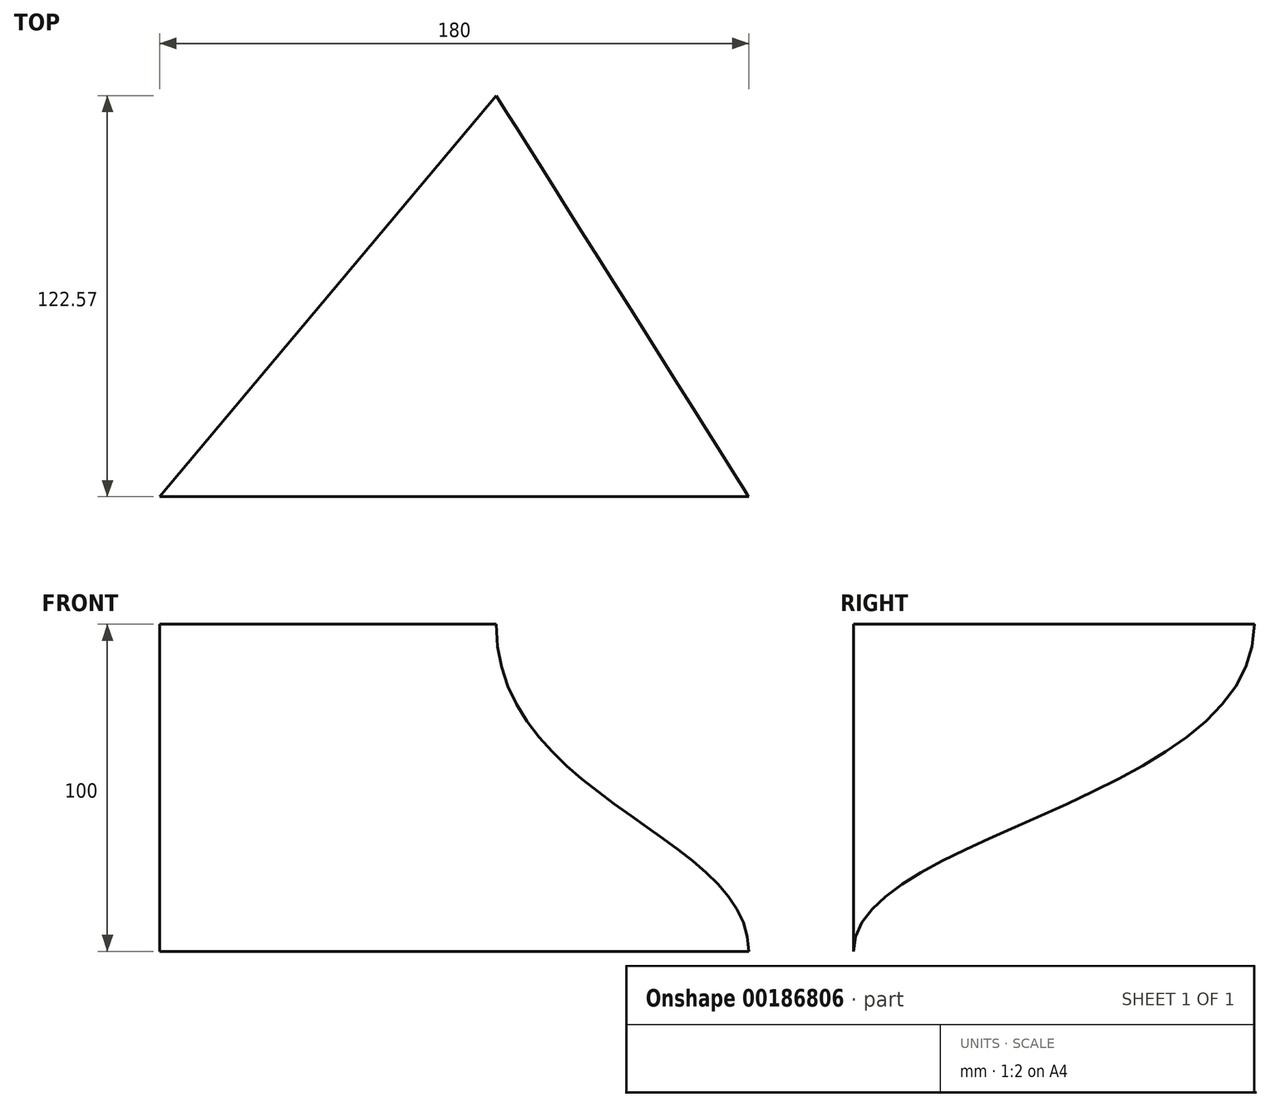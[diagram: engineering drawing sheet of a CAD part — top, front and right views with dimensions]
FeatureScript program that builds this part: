
annotation { "Feature Type Name" : "Feature", "Feature Type Description" : "" }
export const myFeature = defineFeature(function(context is Context, id is Id, definition is map)
    precondition{}
    {
        {
            var Q0;
            Q0=qCreatedBy(makeId("Top.planeOp"),FACE);
            var sketch = newSketch(context, id + "F0", { "sketchPlane" : qUnion([Q0])});
            skLineSegment(sketch, "E0", {"start": v(0, 0) * mm, "end": v(180, 0) * mm});
            skSolve(sketch);
        }
        {
            var Q0;
            Q0=qCreatedBy(makeId("Top.planeOp"),FACE);
            cPlane(context, id + "F1", {"entities" : qUnion([Q0]), "cplaneType" : CPlaneType.OFFSET, "offset" : 100 * mm, "width" : 150 * mm, "height" : 150 * mm});
        }
        {
            var Q0;
            Q0=qCreatedBy(id+"F1.planeOp",FACE);
            var sketch = newSketch(context, id + "F2", { "sketchPlane" : qUnion([Q0])});
            skLineSegment(sketch, "E1", {"start": v(0, 0) * mm, "end": v(102.85, 122.57) * mm});
            skSolve(sketch);
        }
        {
            var Q0;
            Q0=sQuery(id+"F0.wireOp",EDGE,"E0");
            var Q1;
            Q1=sQuery(id+"F2.wireOp",EDGE,"E1");
            loft(context, id + "F3", {"bodyType" : ToolBodyType.SURFACE, "startCondition" : LoftEndDerivativeType.NORMAL_TO_PROFILE, "startMagnitude" : 1, "endCondition" : LoftEndDerivativeType.NORMAL_TO_PROFILE, "endMagnitude" : 1.5, "wireProfilesArray" : [{ "wireProfileEntities" : qUnion([Q0]) }, { "wireProfileEntities" : qUnion([Q1]) }]});
        }
    });
